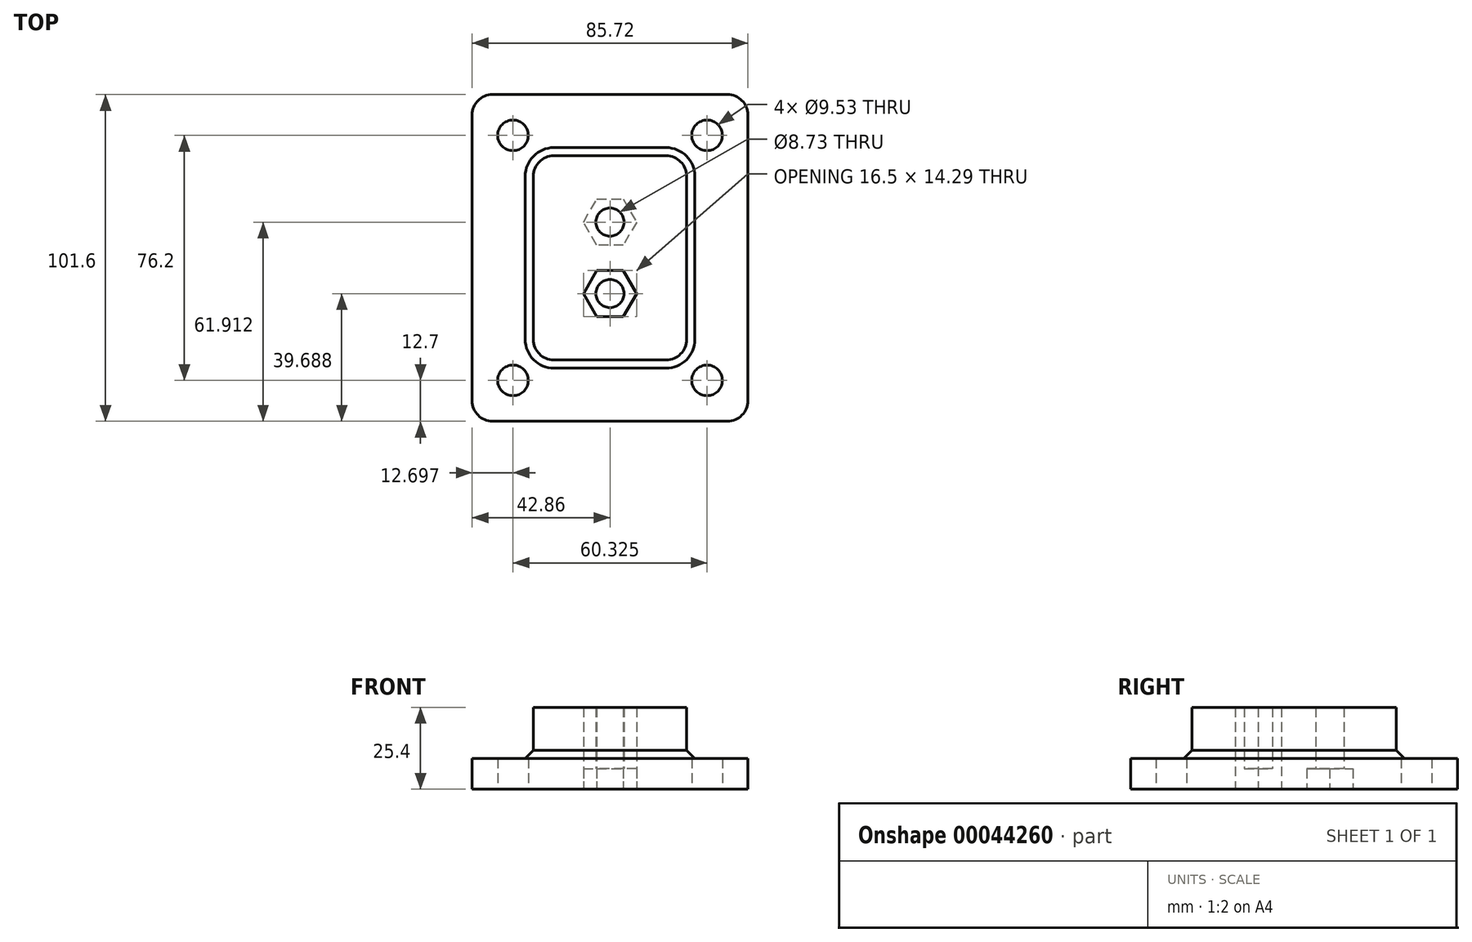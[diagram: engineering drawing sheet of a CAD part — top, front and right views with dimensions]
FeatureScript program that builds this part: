
annotation { "Feature Type Name" : "Feature", "Feature Type Description" : "" }
export const myFeature = defineFeature(function(context is Context, id is Id, definition is map)
    precondition{}
    {
        {
            var Q0;
            Q0=qCreatedBy(makeId("Top.planeOp"),FACE);
            var sketch = newSketch(context, id + "F0", { "sketchPlane" : qUnion([Q0])});
            skLineSegment(sketch, "E0.rect.bottom", {"start": v(-36.51, 50.8) * mm, "end": v(36.51, 50.8) * mm});
            skLineSegment(sketch, "E0.rect.top", {"start": v(-36.51, -50.8) * mm, "end": v(36.51, -50.8) * mm});
            skLineSegment(sketch, "E0.rect.left", {"start": v(-42.86, 44.45) * mm, "end": v(-42.86, -44.45) * mm});
            skLineSegment(sketch, "E0.rect.right", {"start": v(42.86, 44.45) * mm, "end": v(42.86, -44.45) * mm});
            skPoint(sketch, "E0.rect.middle", {"position": v(0, 0) * mm});
            skCircle(sketch, "E1", {"center": v(-30.16, 38.1) * mm, "radius": 4.76 * mm});
            skLineSegment(sketch, "E2", {"start": v(0, 50.8) * mm, "end": v(0, -50.8) * mm, "construction": true});
            skLineSegment(sketch, "E3", {"start": v(-42.86, 0) * mm, "end": v(42.86, 0) * mm, "construction": true});
            skCircle(sketch, "E4.MirrorC", {"center": v(30.16, 38.1) * mm, "radius": 4.76 * mm});
            skCircle(sketch, "E5.MirrorC", {"center": v(-30.16, -38.1) * mm, "radius": 4.76 * mm});
            skCircle(sketch, "E6.MirrorC", {"center": v(30.16, -38.1) * mm, "radius": 4.76 * mm});
            skPoint(sketch, "E7.visualSharp", {"position": v(42.86, 50.8) * mm});
            skArc(sketch, "E7.filletArc", {"start": v(42.86, 44.45) * mm, "mid": v(41, 48.94) * mm, "end": v(36.51, 50.8) * mm});
            skPoint(sketch, "E8.visualSharp", {"position": v(42.86, -50.8) * mm});
            skArc(sketch, "E8.filletArc", {"start": v(36.51, -50.8) * mm, "mid": v(41, -48.94) * mm, "end": v(42.86, -44.45) * mm});
            skPoint(sketch, "E9.visualSharp", {"position": v(-42.86, 50.8) * mm});
            skArc(sketch, "E9.filletArc", {"start": v(-36.51, 50.8) * mm, "mid": v(-41, 48.94) * mm, "end": v(-42.86, 44.45) * mm});
            skPoint(sketch, "E10.visualSharp", {"position": v(-42.86, -50.8) * mm});
            skArc(sketch, "E10.filletArc", {"start": v(-42.86, -44.45) * mm, "mid": v(-41, -48.94) * mm, "end": v(-36.51, -50.8) * mm});
            skCircle(sketch, "E11", {"center": v(0, 11.11) * mm, "radius": 4.37 * mm});
            skCircle(sketch, "E12.MirrorC", {"center": v(0, -11.11) * mm, "radius": 4.37 * mm});
            skLineSegment(sketch, "E13.0", {"start": v(-17.46, 31.75) * mm, "end": v(17.46, 31.75) * mm});
            skLineSegment(sketch, "E13.1", {"start": v(-23.81, 25.4) * mm, "end": v(-23.81, -25.4) * mm});
            skLineSegment(sketch, "E13.2", {"start": v(-17.46, -31.75) * mm, "end": v(17.46, -31.75) * mm});
            skLineSegment(sketch, "E13.3", {"start": v(23.81, 25.4) * mm, "end": v(23.81, -25.4) * mm});
            skPoint(sketch, "E14.visualSharp", {"position": v(-23.81, 31.75) * mm});
            skArc(sketch, "E14.filletArc", {"start": v(-17.46, 31.75) * mm, "mid": v(-21.95, 29.9) * mm, "end": v(-23.81, 25.4) * mm});
            skPoint(sketch, "E15.visualSharp", {"position": v(23.81, 31.75) * mm});
            skArc(sketch, "E15.filletArc", {"start": v(23.81, 25.4) * mm, "mid": v(21.95, 29.9) * mm, "end": v(17.46, 31.75) * mm});
            skPoint(sketch, "E16.visualSharp", {"position": v(23.81, -31.75) * mm});
            skArc(sketch, "E16.filletArc", {"start": v(17.46, -31.75) * mm, "mid": v(21.95, -29.9) * mm, "end": v(23.81, -25.4) * mm});
            skPoint(sketch, "E17.visualSharp", {"position": v(-23.81, -31.75) * mm});
            skArc(sketch, "E17.filletArc", {"start": v(-23.81, -25.4) * mm, "mid": v(-21.95, -29.9) * mm, "end": v(-17.46, -31.75) * mm});
            skCircle(sketch, "E18.cCircle", {"center": v(0, -11.11) * mm, "radius": 7.14 * mm, "construction": true});
            skLineSegment(sketch, "E18.0", {"start": v(4.12, -18.26) * mm, "end": v(-4.12, -18.26) * mm});
            skLineSegment(sketch, "E18.1", {"start": v(-4.12, -18.26) * mm, "end": v(-8.25, -11.11) * mm});
            skLineSegment(sketch, "E18.2", {"start": v(-8.25, -11.11) * mm, "end": v(-4.12, -3.97) * mm});
            skLineSegment(sketch, "E18.3", {"start": v(-4.12, -3.97) * mm, "end": v(4.12, -3.97) * mm});
            skLineSegment(sketch, "E18.4", {"start": v(4.12, -3.97) * mm, "end": v(8.25, -11.11) * mm});
            skLineSegment(sketch, "E18.5", {"start": v(8.25, -11.11) * mm, "end": v(4.12, -18.26) * mm});
            skPoint(sketch, "E18.0.midPoint", {"position": v(0, -18.26) * mm});
            skCircle(sketch, "E19.cCircle", {"center": v(0, 11.11) * mm, "radius": 7.14 * mm, "construction": true});
            skLineSegment(sketch, "E19.0", {"start": v(-4.12, 18.26) * mm, "end": v(4.12, 18.26) * mm});
            skLineSegment(sketch, "E19.1", {"start": v(4.12, 18.26) * mm, "end": v(8.25, 11.11) * mm});
            skLineSegment(sketch, "E19.2", {"start": v(8.25, 11.11) * mm, "end": v(4.12, 3.97) * mm});
            skLineSegment(sketch, "E19.3", {"start": v(4.12, 3.97) * mm, "end": v(-4.12, 3.97) * mm});
            skLineSegment(sketch, "E19.4", {"start": v(-4.12, 3.97) * mm, "end": v(-8.25, 11.11) * mm});
            skLineSegment(sketch, "E19.5", {"start": v(-8.25, 11.11) * mm, "end": v(-4.12, 18.26) * mm});
            skPoint(sketch, "E19.0.midPoint", {"position": v(0, 18.26) * mm});
            skSolve(sketch);
        }
        {
            var Q0;
            Q0=makeQuery(id+"F0.imprint","IMPRINT",FACE,{"disambiguationData":[TD([[makeQuery(id+"F0.imprint","IMPRINT",EDGE,{"derivedFrom":sQuery(id+"F0.wireOp",EDGE,"E12.MirrorC")}),1.0]])]});
            var Q1;
            Q1=makeQuery(id+"F0.imprint","IMPRINT",FACE,{"disambiguationData":[TD([[makeQuery(id+"F0.imprint","IMPRINT",EDGE,{"derivedFrom":sQuery(id+"F0.wireOp",EDGE,"E13.0")}),-1.0]])]});
            var Q2;
            Q2=makeQuery(id+"F0.imprint","IMPRINT",FACE,{"disambiguationData":[TD([[makeQuery(id+"F0.imprint","IMPRINT",EDGE,{"derivedFrom":sQuery(id+"F0.wireOp",EDGE,"E0.rect.bottom")}),-1.0]])]});
            var Q3;
            Q3=makeQuery(id+"F0.imprint","IMPRINT",FACE,{"disambiguationData":[TD([[makeQuery(id+"F0.imprint","IMPRINT",EDGE,{"derivedFrom":sQuery(id+"F0.wireOp",EDGE,"E11")}),-1.0]])]});
            extrude(context, id + "F1", {"entities" : qUnion([Q0, Q1, Q2, Q3]), "depth" : 9.52 * mm});
        }
        {
            var Q0;
            Q0=makeQuery(id+"F0.imprint","IMPRINT",FACE,{"disambiguationData":[TD([[makeQuery(id+"F0.imprint","IMPRINT",EDGE,{"derivedFrom":sQuery(id+"F0.wireOp",EDGE,"E13.0")}),-1.0]])]});
            var Q1;
            Q1=makeQuery(id+"F0.imprint","IMPRINT",FACE,{"disambiguationData":[TD([[makeQuery(id+"F0.imprint","IMPRINT",EDGE,{"derivedFrom":sQuery(id+"F0.wireOp",EDGE,"E11")}),-1.0]])]});
            var Q2;
            Q2=makeQuery(id+"F0.imprint","IMPRINT",FACE,{"disambiguationData":[TD([[makeQuery(id+"F0.imprint","IMPRINT",EDGE,{"derivedFrom":sQuery(id+"F0.wireOp",EDGE,"E12.MirrorC")}),1.0]])]});
            extrude(context, id + "F2", {"entities" : qUnion([Q0, Q1, Q2]), "operationType" : NewBodyOperationType.ADD, "depth" : 25.4 * mm});
        }
        {
            var Q0;
            Q0=makeQuery(id+"F2.boolean.opBoolean","INTERSECT",EDGE,{"derivedFrom":[makeQuery(id+"F1.opExtrude","CAP_FACE",FACE,{"disambiguationData":[OSD([sQuery(id+"F0.wireOp",EDGE,"E0.rect.bottom"),sQuery(id+"F0.wireOp",EDGE,"E0.rect.top"),sQuery(id+"F0.wireOp",EDGE,"E0.rect.left"),sQuery(id+"F0.wireOp",EDGE,"E0.rect.right"),sQuery(id+"F0.wireOp",EDGE,"E1"),sQuery(id+"F0.wireOp",EDGE,"E4.MirrorC"),sQuery(id+"F0.wireOp",EDGE,"E5.MirrorC"),sQuery(id+"F0.wireOp",EDGE,"E6.MirrorC"),sQuery(id+"F0.wireOp",EDGE,"E7.filletArc"),sQuery(id+"F0.wireOp",EDGE,"E8.filletArc"),sQuery(id+"F0.wireOp",EDGE,"E9.filletArc"),sQuery(id+"F0.wireOp",EDGE,"E10.filletArc"),sQuery(id+"F0.wireOp",EDGE,"E11"),sQuery(id+"F0.wireOp",EDGE,"E12.MirrorC")])],"isStart":false}),makeQuery(id+"F2.opExtrude","SWEPT_FACE",FACE,{"disambiguationData":[OSD([sQuery(id+"F0.wireOp",EDGE,"E13.3")])]})]});
            chamfer(context, id + "F3", {"entities" : qUnion([Q0]), "width" : 2.54 * mm, "tangentPropagation" : true});
        }
        {
            var Q0;
            Q0=makeQuery(id+"F0.imprint","IMPRINT",FACE,{"disambiguationData":[TD([[makeQuery(id+"F0.imprint","IMPRINT",EDGE,{"derivedFrom":sQuery(id+"F0.wireOp",EDGE,"E11")}),-1.0]])]});
            var Q1;
            Q1=makeQuery(id+"F0.imprint","IMPRINT",FACE,{"disambiguationData":[TD([[makeQuery(id+"F0.imprint","IMPRINT",EDGE,{"derivedFrom":sQuery(id+"F0.wireOp",EDGE,"E12.MirrorC")}),1.0]])]});
            extrude(context, id + "F4", {"entities" : qUnion([Q0, Q1]), "operationType" : NewBodyOperationType.REMOVE, "depth" : 6.35 * mm});
        }
    });
